# Revit family: Sanitary_Taps-Mixers_AXOR_36133SGP-AXOR-Citterio-E-Single-lever-ba_new
name_source: partatom
category: Plumbing Fixtures
revit_build: Autodesk Revit 2018 (Build: 20170223_1515(x64)
units: mm (PartAtom-declared; Revit-internal decimal feet)

## family parameters
Always vertical = No
Cut with Voids When Loaded = No
OmniClass Number = 23.31.11.00
OmniClass Title = Faucets
Part Type = Normal
Room Calculation Point = No
Round Connector Dimension = Use Diameter
Shared = No
Work Plane-Based = Yes

## types (1)
- 009 Matt Black
    Always visible = Yes
    BIMobject category = Taps & Mixers
    Default Elevation = 1219.2 mm  [stored 4 ft]
    Description = AXOR Citterio E Single lever basin mixer for concealed installation wall-mounted with spout 221 mm and plate 2 ticks
    Design country = Germany
    EAN code = 4059625274774
    Edition number = 1
    GTIN code = https://4059625274774
    IFC Classification = Valve
    Manufacturer = AXOR
    Manufacturer country = Germany
    Manufacturer name = AXOR
    Material 1 = AXOR - Metal - 009 Matt Black
    Model = 36133SGP
    OmniClass Code = 23-31 11 00
    OmniClass Description = Faucets
    Product Guid = 49736314-e61a-47a6-87a9-4e2b1b4969cb
    Product SKU = 36133SGP
    Product data url = https://bimobject.com
    Product family = AXOR Citterio E
    Product group = Basin mixers
    Product name = 36133SGP AXOR Citterio E Single lever basin mixer for concealed installation wall-mounted with spout 221 mm and plate 2 ticks
    QR code = https://bimobject.com
    URL = https://www.axor-design.com
    Weight Net (Kg) = 1.9

note: [stored X ft] marks values corroborated as IEEE doubles in the binary element streams (Revit-internal decimal feet)

## geometry (parser evidence)
native form markers: Sweep x1
no freeform markers — native parametric forms only
